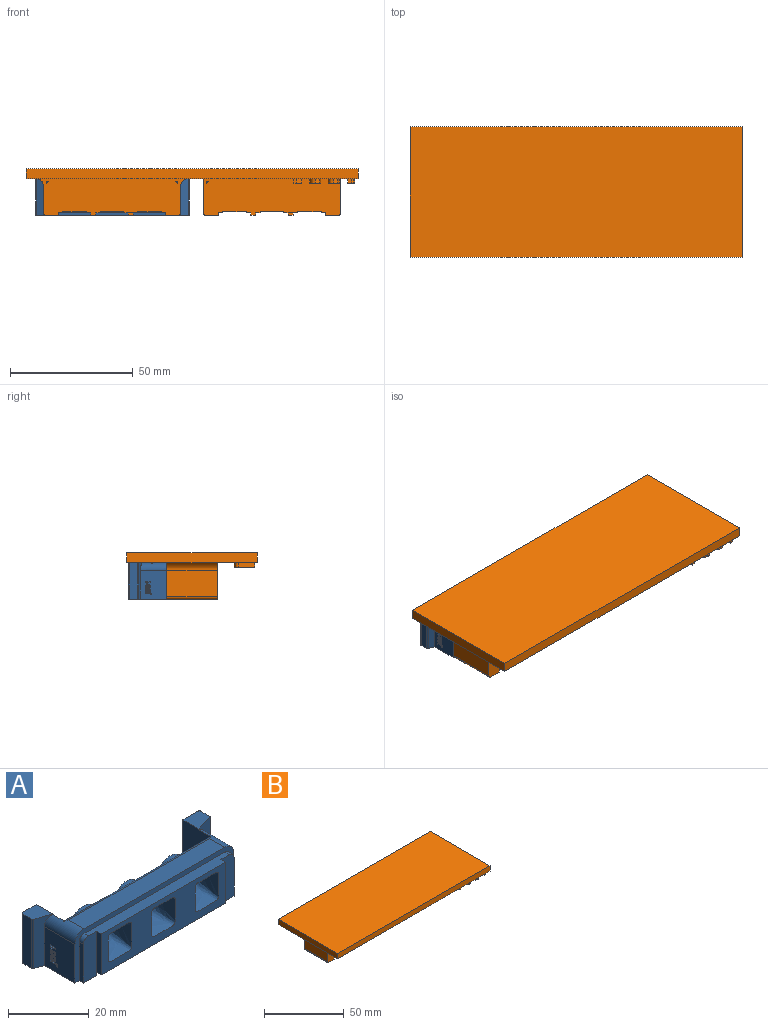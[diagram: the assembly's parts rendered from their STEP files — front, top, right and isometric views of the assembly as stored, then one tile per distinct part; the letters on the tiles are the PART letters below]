
ASSEMBLY  parts=2 mates=1
PART A: 118 faces, bbox 63x19.4x15.4 mm
  f0: plane 11.78x10.74mm, normal (-1,0,0), area 119.5mm2, adj f11,f26,f39,f49,f60,f61,f62,f63
  f1: plane 44.18x12.95mm, normal (0,-1,0), area 333.4mm2, adj f4,f54,f55,f56,f57,f58,f59
  f2: plane 13.48x4.58mm, normal (0,-1,0), area 61.1mm2, adj f4,f11,f45,f46,f47,f56
  f3: cylinder r=1.7mm len=1.7mm, axis (0,-1,0), area 4mm2, adj f4,f21,f48,f49
  f4: plane 49.45x3.15mm, normal (0,0,1), area 146.3mm2, adj f1,f2,f3,f21,f46,f49,f55,f56
  f5: plane 2.03x1.02mm, normal (0,-1,0), area 2.1mm2, adj f11,f43,f44,f54
  f6: plane 2.03x1.02mm, normal (0,-1,0), area 2.1mm2, adj f11,f41,f42,f54
  f7: cylinder r=3.17mm len=6.35mm, axis (0,-1,0), area 89.2mm2, adj f30,f57
  f8: cylinder r=3.17mm len=6.35mm, axis (0,-1,0), area 89.2mm2, adj f34,f59
  f9: cylinder r=3.17mm len=6.35mm, axis (0,-1,0), area 89.2mm2, adj f32,f58
  f10: plane 11.78x10.74mm, normal (1,0,0), area 126.5mm2, adj f11,f27,f38,f49
  f11: plane 62.5x17.24mm, normal (0,0,-1), area 324.6mm2, adj f0,f2,f5,f6,f10,f12,f14,f16
  f12: plane 13.21x1.02mm, normal (0,-1,0), area 13.4mm2, adj f11,f13,f44,f45
  f13: plane 13.21x4.57mm, normal (0,0,-1), area 60.4mm2, adj f12,f44,f45,f54
  f14: plane 13.21x1.02mm, normal (0,-1,0), area 13.4mm2, adj f11,f15,f42,f43
  f15: plane 13.21x4.57mm, normal (0,0,-1), area 60.4mm2, adj f14,f42,f43,f54
  f16: plane 13.21x1.02mm, normal (0,-1,0), area 13.4mm2, adj f11,f17,f40,f41
  f17: plane 13.21x4.57mm, normal (0,0,-1), area 60.4mm2, adj f16,f40,f41,f54
  f18: plane 49.45x5.36mm, normal (0,0,1), area 265mm2, adj f37,f38,f39,f49
  f19: plane 5.69x5.33mm, normal (0,0,1), area 25.7mm2, adj f22,f25,f26,f29,f51,f52
  f20: plane 51.44x13.94mm, normal (0,1,0), area 530.7mm2, adj f11,f22,f23,f31,f33,f35,f37
  f21: plane 13.48x4.58mm, normal (0,-1,0), area 61.1mm2, adj f3,f4,f11,f40,f48,f55
  f22: plane 14.95x9.83mm, normal (1,0,0), area 139.5mm2, adj f11,f19,f20,f26,f37,f39,f51
  f23: plane 14.95x9.83mm, normal (-1,0,0), area 139.5mm2, adj f11,f20,f27,f36,f37,f38,f50
  f24: plane 14.95x3.11mm, normal (1,0,0), area 46.5mm2, adj f11,f28,f36,f53
  f25: plane 14.95x3.12mm, normal (-1,0,0), area 46.7mm2, adj f11,f19,f29,f52
  f26: plane 15.27x5.29mm, normal (-0.3,-0.95,0), area 46mm2, adj f0,f11,f19,f22,f29,f39
  f27: plane 15.23x5.64mm, normal (0.27,-0.96,0), area 51.6mm2, adj f10,f11,f23,f28,f36,f38
  f28: cylinder r=0.51mm len=14.95mm, axis (0,0,-1), area 9.8mm2, adj f11,f24,f27,f36
  f29: cylinder r=0.51mm len=14.95mm, axis (0,0,-1), area 9.6mm2, adj f11,f19,f25,f26
  f30: plane 8.89x8.89mm, normal (0,1,0), area 30.4mm2, adj f7,f31
  f31: cylinder r=4.45mm len=8.89mm, axis (0,-1,0), area 96.5mm2, adj f20,f30
  f32: plane 8.89x8.89mm, normal (0,1,0), area 30.4mm2, adj f9,f33
  f33: cylinder r=4.45mm len=8.89mm, axis (0,-1,0), area 96.5mm2, adj f20,f32
  f34: plane 8.89x8.89mm, normal (0,1,0), area 30.4mm2, adj f8,f35
  f35: cylinder r=4.45mm len=8.89mm, axis (0,-1,0), area 96.5mm2, adj f20,f34
  f36: plane 5.74x5.61mm, normal (0,0,1), area 27.5mm2, adj f23,f24,f27,f28,f50,f53
  f37: cylinder r=1.02mm len=51.44mm, axis (1,0,0), area 81.5mm2, adj f18,f20,f22,f23,f38,f39
  f38: cylinder r=3.17mm len=10.74mm, axis (0,-1,0), area 47.2mm2, adj f10,f18,f23,f27,f37,f49
  f39: cylinder r=3.17mm len=10.74mm, axis (0,1,0), area 47mm2, adj f0,f18,f22,f26,f37,f49
  f40: plane 4.57x1.02mm, normal (1,0,0), area 4.6mm2, adj f11,f16,f17,f21
  f41: plane 4.57x1.02mm, normal (-1,0,0), area 4.6mm2, adj f6,f11,f16,f17
  f42: plane 4.57x1.02mm, normal (1,0,0), area 4.6mm2, adj f6,f11,f14,f15
  f43: plane 4.57x1.02mm, normal (-1,0,0), area 4.6mm2, adj f5,f11,f14,f15
  f44: plane 4.57x1.02mm, normal (1,0,0), area 4.6mm2, adj f5,f11,f12,f13
  f45: plane 4.57x1.02mm, normal (-1,0,0), area 4.6mm2, adj f2,f11,f12,f13
  f46: cylinder r=1.7mm len=1.7mm, axis (0,-1,0), area 4mm2, adj f2,f4,f47,f49
  f47: plane 11.78x1.5mm, normal (1,0,0), area 17.7mm2, adj f2,f11,f46,f49
  f48: plane 11.78x1.5mm, normal (-1,0,0), area 17.7mm2, adj f3,f11,f21,f49
  f49: plane 55.8x14.95mm, normal (0,-1,0), area 119mm2, adj f0,f3,f4,f10,f11,f18,f38,f39
  f50: plane 14.95x5.23mm, normal (0,1,0), area 78.2mm2, adj f11,f23,f36,f53
  f51: plane 14.95x4.82mm, normal (0,1,0), area 72.1mm2, adj f11,f19,f22,f52
  f52: cylinder r=0.51mm len=14.95mm, axis (0,0,-1), area 11.9mm2, adj f11,f19,f25,f51
  f53: cylinder r=0.51mm len=14.95mm, axis (0,0,-1), area 11.9mm2, adj f11,f24,f36,f50
  f54: plane 43.69x1.65mm, normal (0,0,-1), area 72.1mm2, adj f1,f5,f6,f13,f15,f17,f55,f56
  f55: plane 12.46x1.65mm, normal (-1,0,0), area 20.6mm2, adj f1,f4,f21,f54
  f56: plane 12.46x1.65mm, normal (1,0,0), area 20.6mm2, adj f1,f2,f4,f54
  f57: bspline ~8.64x8.51mm, area 223.4mm2, adj f1,f7
  f58: bspline ~8.64x8.51mm, area 223.4mm2, adj f1,f9
  f59: bspline ~8.64x8.51mm, area 223.4mm2, adj f1,f8
  f60: plane 1x0.42mm, normal (0,1,0), area 0.4mm2, adj f0,f61,f69,f70
  f61: plane 1.98x1mm, normal (0,0,-1), area 2mm2, adj f0,f60,f62,f70
  f62: plane 1x0.34mm, normal (0,-1,0), area 0.3mm2, adj f0,f61,f63,f70
  f63: plane 1x0.64mm, normal (0,-0.78,0.62), area 0.8mm2, adj f0,f62,f64,f70
  f64: plane 1x0.25mm, normal (0,0.63,0.78), area 0.3mm2, adj f0,f63,f65,f70
  f65: plane 1x0.23mm, normal (0,0.78,-0.63), area 0.3mm2, adj f0,f64,f66,f70
  f66: extruded ~1x0.15mm, area 0.2mm2, adj f0,f65,f67,f70
  f67: plane 1x0.21mm, normal (0,-0.03,1), area 0.2mm2, adj f0,f66,f68,f70
  f68: plane 1x0.19mm, normal (0,-0.02,1), area 0.2mm2, adj f0,f67,f69,f70
  f69: plane 1.15x1mm, normal (0,0,1), area 1.1mm2, adj f0,f60,f68,f70
  f70: plane 1.98x0.98mm, normal (-1,0,0), area 1mm2, adj f60,f61,f62,f63,f64,f65,f66,f67
  f71: extruded ~1x0.52mm, area 0.5mm2, adj f72,f86,f87,f116
  f72: extruded ~1x0.52mm, area 0.5mm2, adj f71,f73,f87,f116
  f73: extruded ~1x0.21mm, area 0.3mm2, adj f72,f74,f87,f116
  f74: extruded ~1x0.21mm, area 0.3mm2, adj f73,f75,f87,f116
  f75: extruded ~1x0.52mm, area 0.5mm2, adj f74,f76,f87,f116
  f76: extruded ~1x0.52mm, area 0.5mm2, adj f75,f77,f87,f116
  f77: extruded ~1x0.21mm, area 0.3mm2, adj f76,f86,f87,f116
  f78: extruded ~1x0.77mm, area 0.8mm2, adj f0,f79,f85,f87
  f79: extruded ~1x0.76mm, area 0.8mm2, adj f0,f78,f80,f87
  f80: extruded ~1x0.52mm, area 0.6mm2, adj f0,f79,f81,f87
  f81: extruded ~1x0.52mm, area 0.6mm2, adj f0,f80,f82,f87
  f82: extruded ~1x0.77mm, area 0.8mm2, adj f0,f81,f83,f87
  f83: extruded ~1x0.76mm, area 0.8mm2, adj f0,f82,f84,f87
  f84: extruded ~1x0.52mm, area 0.6mm2, adj f0,f83,f85,f87
  f85: extruded ~1x0.52mm, area 0.6mm2, adj f0,f78,f84,f87
  f86: extruded ~1x0.21mm, area 0.3mm2, adj f71,f77,f87,f116
  f87: plane 2.04x1.39mm, normal (-1,0,0), area 1.7mm2, adj f71,f72,f73,f74,f75,f76,f77,f78
  f88: extruded ~1x0.52mm, area 0.5mm2, adj f89,f103,f104,f117
  f89: extruded ~1x0.52mm, area 0.5mm2, adj f88,f90,f104,f117
  f90: extruded ~1x0.21mm, area 0.3mm2, adj f89,f91,f104,f117
  f91: extruded ~1x0.21mm, area 0.3mm2, adj f90,f92,f104,f117
  f92: extruded ~1x0.52mm, area 0.5mm2, adj f91,f93,f104,f117
  f93: extruded ~1x0.52mm, area 0.5mm2, adj f92,f94,f104,f117
  f94: extruded ~1x0.21mm, area 0.3mm2, adj f93,f103,f104,f117
  f95: extruded ~1x0.77mm, area 0.8mm2, adj f0,f96,f102,f104
  f96: extruded ~1x0.76mm, area 0.8mm2, adj f0,f95,f97,f104
  f97: extruded ~1x0.52mm, area 0.6mm2, adj f0,f96,f98,f104
  f98: extruded ~1x0.52mm, area 0.6mm2, adj f0,f97,f99,f104
  f99: extruded ~1x0.77mm, area 0.8mm2, adj f0,f98,f100,f104
  f100: extruded ~1x0.76mm, area 0.8mm2, adj f0,f99,f101,f104
  f101: extruded ~1x0.52mm, area 0.6mm2, adj f0,f100,f102,f104
  f102: extruded ~1x0.52mm, area 0.6mm2, adj f0,f95,f101,f104
  f103: extruded ~1x0.21mm, area 0.3mm2, adj f88,f94,f104,f117
  f104: plane 2.04x1.39mm, normal (-1,0,0), area 1.7mm2, adj f88,f89,f90,f91,f92,f93,f94,f95
  f105: extruded ~1x0.25mm, area 0.3mm2, adj f0,f106,f114,f115
  f106: extruded ~1x0.47mm, area 0.5mm2, adj f0,f105,f107,f115
  f107: extruded ~1x0.53mm, area 0.6mm2, adj f0,f106,f108,f115
  f108: plane 1.86x1mm, normal (0,0,-1), area 1.9mm2, adj f0,f107,f109,f115
  f109: plane 1x0.42mm, normal (0,-1,0), area 0.4mm2, adj f0,f108,f110,f115
  f110: plane 1.86x1mm, normal (0,0,1), area 1.9mm2, adj f0,f109,f111,f115
  f111: extruded ~1x0.27mm, area 0.3mm2, adj f0,f110,f112,f115
  f112: extruded ~1x0.2mm, area 0.2mm2, adj f0,f111,f113,f115
  f113: extruded ~1x0.2mm, area 0.2mm2, adj f0,f112,f114,f115
  f114: plane 1x0.35mm, normal (0,0,1), area 0.3mm2, adj f0,f105,f113,f115
  f115: plane 2.57x0.88mm, normal (-1,0,0), area 1.2mm2, adj f105,f106,f107,f108,f109,f110,f111,f112
  f116: plane 1.36x0.55mm, normal (-1,0,0), area 0.6mm2, adj f71,f72,f73,f74,f75,f76,f77,f86
  f117: plane 1.36x0.55mm, normal (-1,0,0), area 0.6mm2, adj f88,f89,f90,f91,f92,f93,f94,f103
PART B: 188 faces, bbox 135.1x53.1x19.1 mm
  f0: plane 135x53mm, normal (0,0,-1), area 4658.1mm2, adj f20,f61,f81,f82,f83,f122,f123,f124
  f1: plane 43.69x13.68mm, normal (0,1,0), area 279.1mm2, adj f2,f5,f7,f8,f9,f10,f12,f13
  f2: plane 53.24x3.15mm, normal (0,0,-1), area 152mm2, adj f1,f3,f6,f14,f36,f55,f57,f61
  f3: plane 13.68x4.78mm, normal (0,1,0), area 65.3mm2, adj f2,f31,f36,f55
  f4: torus R=2.16mm, axis (0,1,0), area 0.4mm2, adj f20,f56,f58
  f5: plane 17.4x1.78mm, normal (0,0,-1), area 30.9mm2, adj f1,f7,f14,f20
  f6: plane 13.68x4.78mm, normal (0,1,0), area 65.3mm2, adj f2,f11,f14,f57
  f7: plane 17.4x0.43mm, normal (1,0,0), area 7.5mm2, adj f1,f5,f20,f25
  f8: plane 17.4x0.43mm, normal (-1,0,0), area 7.5mm2, adj f1,f12,f20,f29
  f9: plane 17.4x0.43mm, normal (1,0,0), area 7.5mm2, adj f1,f12,f20,f30
  f10: plane 17.4x0.43mm, normal (-1,0,0), area 7.5mm2, adj f1,f13,f20,f30
  f11: plane 20.55x5.04mm, normal (0,0,-1), area 96.4mm2, adj f6,f14,f20,f41,f57,f61
  f12: plane 17.4x5.59mm, normal (0,0,-1), area 61.9mm2, adj f1,f8,f9,f20,f49,f50,f51
  f13: plane 17.4x1.78mm, normal (0,0,-1), area 30.9mm2, adj f1,f10,f20,f36
  f14: plane 19.05x13.68mm, normal (1,0,0), area 40.3mm2, adj f1,f2,f5,f6,f11,f20
  f15: plane 14.25x10.51mm, normal (-1,0.02,0), area 126.2mm2, adj f1,f26,f30,f32,f44,f47
  f16: plane 14.25x10.51mm, normal (1,0.02,0), area 126.2mm2, adj f1,f26,f30,f32,f44,f47
  f17: plane 14.25x10.51mm, normal (-1,0.02,0), area 126.2mm2, adj f1,f27,f29,f33,f43,f46
  f18: plane 14.25x10.51mm, normal (1,0.02,0), area 126.2mm2, adj f1,f27,f29,f33,f43,f46
  f19: plane 14.25x10.51mm, normal (-1,0.02,0), area 126.2mm2, adj f1,f25,f28,f35,f42,f45
  f20: plane 62.15x14.95mm, normal (0,-1,0), area 782.9mm2, adj f0,f4,f5,f7,f8,f9,f10,f11
  f21: plane 20.55x10.76mm, normal (-1,0,0), area 221.2mm2, adj f20,f41,f61,f187
  f22: plane 20.55x10.76mm, normal (1,0,0), area 221.2mm2, adj f20,f39,f61,f186
  f23: plane 17.4x0.43mm, normal (-1,0,0), area 7.5mm2, adj f1,f20,f25,f37
  f24: plane 17.4x0.43mm, normal (1,0,0), area 7.5mm2, adj f1,f20,f29,f38
  f25: plane 17.4x9.65mm, normal (0,0,-1), area 51.3mm2, adj f1,f7,f19,f20,f23,f34,f35
  f26: plane 8.45x0.86mm, normal (0,0.02,-1), area 7.3mm2, adj f1,f15,f16,f44
  f27: plane 8.45x0.86mm, normal (0,0.02,-1), area 7.3mm2, adj f1,f17,f18,f43
  f28: plane 8.45x0.86mm, normal (0,0.02,-1), area 7.3mm2, adj f1,f19,f34,f42
  f29: plane 17.4x9.65mm, normal (0,0,-1), area 51.3mm2, adj f1,f8,f17,f18,f20,f24,f33
  f30: plane 17.4x9.65mm, normal (0,0,-1), area 51.3mm2, adj f1,f9,f10,f15,f16,f20,f32
  f31: plane 20.55x5.04mm, normal (0,0,-1), area 96.4mm2, adj f3,f20,f36,f39,f55,f61
  f32: plane 7.95x5.84mm, normal (0,1,0), area 46.4mm2, adj f15,f16,f30,f47
  f33: plane 7.95x5.84mm, normal (0,1,0), area 46.4mm2, adj f17,f18,f29,f46
  f34: plane 14.25x10.51mm, normal (1,0.02,0), area 126.2mm2, adj f1,f25,f28,f35,f42,f45
  f35: plane 7.95x5.84mm, normal (0,1,0), area 46.4mm2, adj f19,f25,f34,f45
  f36: plane 19.05x13.68mm, normal (-1,0,0), area 40.3mm2, adj f1,f2,f3,f13,f20,f31
  f37: plane 17.4x1.78mm, normal (0,0,-1), area 30.9mm2, adj f1,f20,f23,f53
  f38: plane 17.4x1.78mm, normal (0,0,-1), area 30.9mm2, adj f1,f20,f24,f54
  f39: cylinder r=1.02mm len=20.55mm, axis (0,1,0), area 32.8mm2, adj f20,f22,f31,f61
  f40: torus R=2.16mm, axis (0,1,0), area 0.4mm2, adj f20,f59,f60
  f41: cylinder r=1.02mm len=20.55mm, axis (0,-1,0), area 32.8mm2, adj f11,f20,f21,f61
  f42: plane 8.42x5mm, normal (0,0.61,-0.79), area 52.8mm2, adj f19,f28,f34,f45
  f43: plane 8.42x5mm, normal (0,0.61,-0.79), area 52.8mm2, adj f17,f18,f27,f46
  f44: plane 8.42x5mm, normal (0,0.61,-0.79), area 52.8mm2, adj f15,f16,f26,f47
  f45: cylinder r=4.25mm len=8.36mm, axis (1,0,0), area 96.9mm2, adj f19,f34,f35,f42
  f46: cylinder r=4.25mm len=8.36mm, axis (1,0,0), area 96.9mm2, adj f17,f18,f33,f43
  f47: cylinder r=4.25mm len=8.36mm, axis (1,0,0), area 96.9mm2, adj f15,f16,f32,f44
  f48: plane 17.36x2.03mm, normal (0,0,-1), area 35.3mm2, adj f1,f49,f50,f51
  f49: plane 2.03x1.02mm, normal (0,-1,0), area 2.1mm2, adj f12,f48,f50,f51
  f50: plane 17.36x1.02mm, normal (-1,0,0), area 17.6mm2, adj f1,f12,f48,f49
  f51: plane 17.36x1.02mm, normal (1,0,0), area 17.6mm2, adj f1,f12,f48,f49
  f52: plane 17.4x2.03mm, normal (0,0,-1), area 35.4mm2, adj f1,f20,f53,f54
  f53: plane 17.4x1.02mm, normal (-1,0,0), area 17.7mm2, adj f1,f20,f37,f52
  f54: plane 17.4x1.02mm, normal (1,0,0), area 17.7mm2, adj f1,f20,f38,f52
  f55: plane 13.68x1.5mm, normal (-1,0,0), area 20.5mm2, adj f2,f3,f31,f61
  f56: plane 0.98x0.26mm, normal (0,0,-1), area 0mm2, adj f4,f20,f58
  f57: plane 13.68x1.5mm, normal (1,0,0), area 20.5mm2, adj f2,f6,f11,f61
  f58: plane 0.98x0.26mm, normal (-1,0,0), area 0mm2, adj f4,f20,f56
  f59: plane 0.98x0.26mm, normal (0,0,-1), area 0mm2, adj f20,f40,f60
  f60: plane 0.98x0.26mm, normal (1,0,0), area 0mm2, adj f20,f40,f59
  f61: plane 62.15x14.95mm, normal (0,1,0), area 110.2mm2, adj f0,f2,f11,f21,f22,f31,f39,f41
  f62: plane 43.69x13.68mm, normal (0,1,0), area 279.1mm2, adj f63,f66,f68,f69,f70,f71,f73,f74
  f63: plane 53.24x3.15mm, normal (0,0,-1), area 152mm2, adj f62,f64,f67,f75,f97,f116,f118,f122
  f64: plane 13.68x4.78mm, normal (0,1,0), area 65.3mm2, adj f63,f92,f97,f116
  f65: torus R=2.16mm, axis (0,1,0), area 0.4mm2, adj f81,f117,f119
  f66: plane 17.4x1.78mm, normal (0,0,-1), area 30.9mm2, adj f62,f68,f75,f81
  f67: plane 13.68x4.78mm, normal (0,1,0), area 65.3mm2, adj f63,f72,f75,f118
  f68: plane 17.4x0.43mm, normal (1,0,0), area 7.5mm2, adj f62,f66,f81,f86
  f69: plane 17.4x0.43mm, normal (-1,0,0), area 7.5mm2, adj f62,f73,f81,f90
  f70: plane 17.4x0.43mm, normal (1,0,0), area 7.5mm2, adj f62,f73,f81,f91
  f71: plane 17.4x0.43mm, normal (-1,0,0), area 7.5mm2, adj f62,f74,f81,f91
  f72: plane 20.55x5.04mm, normal (0,0,-1), area 96.4mm2, adj f67,f75,f81,f102,f118,f122
  f73: plane 17.4x5.59mm, normal (0,0,-1), area 61.9mm2, adj f62,f69,f70,f81,f110,f111,f112
  f74: plane 17.4x1.78mm, normal (0,0,-1), area 30.9mm2, adj f62,f71,f81,f97
  f75: plane 19.05x13.68mm, normal (1,0,0), area 40.3mm2, adj f62,f63,f66,f67,f72,f81
  f76: plane 14.25x10.51mm, normal (-1,0.02,0), area 126.2mm2, adj f62,f87,f91,f93,f105,f108
  f77: plane 14.25x10.51mm, normal (1,0.02,0), area 126.2mm2, adj f62,f87,f91,f93,f105,f108
  f78: plane 14.25x10.51mm, normal (-1,0.02,0), area 126.2mm2, adj f62,f88,f90,f94,f104,f107
  f79: plane 14.25x10.51mm, normal (1,0.02,0), area 126.2mm2, adj f62,f88,f90,f94,f104,f107
  f80: plane 14.25x10.51mm, normal (-1,0.02,0), area 126.2mm2, adj f62,f86,f89,f96,f103,f106
  f81: plane 55.8x14.95mm, normal (0,-1,0), area 778.6mm2, adj f0,f65,f66,f68,f69,f70,f71,f72
  f82: plane 20.55x13.94mm, normal (-1,0,0), area 286.4mm2, adj f0,f81,f102,f122
  f83: plane 20.55x13.94mm, normal (1,0,0), area 286.4mm2, adj f0,f81,f100,f122
  f84: plane 17.4x0.43mm, normal (-1,0,0), area 7.5mm2, adj f62,f81,f86,f98
  f85: plane 17.4x0.43mm, normal (1,0,0), area 7.5mm2, adj f62,f81,f90,f99
  f86: plane 17.4x9.65mm, normal (0,0,-1), area 51.3mm2, adj f62,f68,f80,f81,f84,f95,f96
  f87: plane 8.45x0.86mm, normal (0,0.02,-1), area 7.3mm2, adj f62,f76,f77,f105
  f88: plane 8.45x0.86mm, normal (0,0.02,-1), area 7.3mm2, adj f62,f78,f79,f104
  f89: plane 8.45x0.86mm, normal (0,0.02,-1), area 7.3mm2, adj f62,f80,f95,f103
  f90: plane 17.4x9.65mm, normal (0,0,-1), area 51.3mm2, adj f62,f69,f78,f79,f81,f85,f94
  f91: plane 17.4x9.65mm, normal (0,0,-1), area 51.3mm2, adj f62,f70,f71,f76,f77,f81,f93
  f92: plane 20.55x5.04mm, normal (0,0,-1), area 96.4mm2, adj f64,f81,f97,f100,f116,f122
  f93: plane 7.95x5.84mm, normal (0,1,0), area 46.4mm2, adj f76,f77,f91,f108
  f94: plane 7.95x5.84mm, normal (0,1,0), area 46.4mm2, adj f78,f79,f90,f107
  f95: plane 14.25x10.51mm, normal (1,0.02,0), area 126.2mm2, adj f62,f86,f89,f96,f103,f106
  f96: plane 7.95x5.84mm, normal (0,1,0), area 46.4mm2, adj f80,f86,f95,f106
  f97: plane 19.05x13.68mm, normal (-1,0,0), area 40.3mm2, adj f62,f63,f64,f74,f81,f92
  f98: plane 17.4x1.78mm, normal (0,0,-1), area 30.9mm2, adj f62,f81,f84,f114
  f99: plane 17.4x1.78mm, normal (0,0,-1), area 30.9mm2, adj f62,f81,f85,f115
  f100: cylinder r=1.02mm len=20.55mm, axis (0,1,0), area 32.8mm2, adj f81,f83,f92,f122
  f101: torus R=2.16mm, axis (0,1,0), area 0.4mm2, adj f81,f120,f121
  f102: cylinder r=1.02mm len=20.55mm, axis (0,-1,0), area 32.8mm2, adj f72,f81,f82,f122
  f103: plane 8.42x5mm, normal (0,0.61,-0.79), area 52.8mm2, adj f80,f89,f95,f106
  f104: plane 8.42x5mm, normal (0,0.61,-0.79), area 52.8mm2, adj f78,f79,f88,f107
  f105: plane 8.42x5mm, normal (0,0.61,-0.79), area 52.8mm2, adj f76,f77,f87,f108
  f106: cylinder r=4.25mm len=8.36mm, axis (1,0,0), area 96.9mm2, adj f80,f95,f96,f103
  f107: cylinder r=4.25mm len=8.36mm, axis (1,0,0), area 96.9mm2, adj f78,f79,f94,f104
  f108: cylinder r=4.25mm len=8.36mm, axis (1,0,0), area 96.9mm2, adj f76,f77,f93,f105
  f109: plane 17.36x2.03mm, normal (0,0,-1), area 35.3mm2, adj f62,f110,f111,f112
  f110: plane 2.03x1.02mm, normal (0,-1,0), area 2.1mm2, adj f73,f109,f111,f112
  f111: plane 17.36x1.02mm, normal (-1,0,0), area 17.6mm2, adj f62,f73,f109,f110
  f112: plane 17.36x1.02mm, normal (1,0,0), area 17.6mm2, adj f62,f73,f109,f110
  f113: plane 17.4x2.03mm, normal (0,0,-1), area 35.4mm2, adj f62,f81,f114,f115
  f114: plane 17.4x1.02mm, normal (-1,0,0), area 17.7mm2, adj f62,f81,f98,f113
  f115: plane 17.4x1.02mm, normal (1,0,0), area 17.7mm2, adj f62,f81,f99,f113
  f116: plane 13.68x1.5mm, normal (-1,0,0), area 20.5mm2, adj f63,f64,f92,f122
  f117: plane 0.98x0.26mm, normal (0,0,-1), area 0mm2, adj f65,f81,f119
  f118: plane 13.68x1.5mm, normal (1,0,0), area 20.5mm2, adj f63,f67,f72,f122
  f119: plane 0.98x0.26mm, normal (-1,0,0), area 0mm2, adj f65,f81,f117
  f120: plane 0.98x0.26mm, normal (0,0,-1), area 0mm2, adj f81,f101,f121
  f121: plane 0.98x0.26mm, normal (1,0,0), area 0mm2, adj f81,f101,f120
  f122: plane 55.8x14.95mm, normal (0,1,0), area 105.8mm2, adj f0,f63,f72,f82,f83,f92,f100,f102
  f123: plane 53x4mm, normal (-1,0,0), area 212mm2, adj f0,f124,f126,f127
  f124: plane 135x4mm, normal (0,-1,0), area 540mm2, adj f0,f123,f125,f127
  f125: plane 53x4mm, normal (1,0,0), area 212mm2, adj f0,f124,f126,f127
  f126: plane 135x4mm, normal (0,1,0), area 540mm2, adj f0,f123,f125,f127
  f127: plane 135x53mm, normal (0,0,1), area 7155mm2, adj f123,f124,f125,f126
  f128: extruded ~2x1.53mm, area 3.4mm2, adj f0,f129,f137,f138
  f129: extruded ~2x0.81mm, area 1.6mm2, adj f0,f128,f130,f138
  f130: plane 2x1.14mm, normal (1,0,0), area 2.3mm2, adj f0,f129,f131,f138
  f131: extruded ~2x0.64mm, area 1.3mm2, adj f0,f130,f132,f138
  f132: extruded ~2x0.64mm, area 1.5mm2, adj f0,f131,f133,f138
  f133: extruded ~2x0.88mm, area 1.8mm2, adj f0,f132,f134,f138
  f134: plane 6.04x2mm, normal (1,0,0), area 12.1mm2, adj f0,f133,f135,f138
  f135: plane 2x1.37mm, normal (0,-1,0), area 2.7mm2, adj f0,f134,f136,f138
  f136: plane 6.03x2mm, normal (-1,0,0), area 12.1mm2, adj f0,f135,f137,f138
  f137: extruded ~2x1.72mm, area 3.7mm2, adj f0,f128,f136,f138
  f138: plane 8.34x2.85mm, normal (0,0,-1), area 12.4mm2, adj f128,f129,f130,f131,f132,f133,f134,f135
  f139: extruded ~2.48x2mm, area 5.2mm2, adj f0,f140,f154,f155
  f140: extruded ~2.5x2mm, area 5.2mm2, adj f0,f139,f141,f155
  f141: extruded ~2x1.7mm, area 3.9mm2, adj f0,f140,f142,f155
  f142: extruded ~2x1.68mm, area 3.9mm2, adj f0,f141,f143,f155
  f143: extruded ~2.47x2mm, area 5.1mm2, adj f0,f142,f144,f155
  f144: extruded ~2.52x2mm, area 5.2mm2, adj f0,f143,f145,f155
  f145: extruded ~2x1.7mm, area 3.9mm2, adj f0,f144,f154,f155
  f146: extruded ~2x1.7mm, area 3.5mm2, adj f147,f153,f155,f156
  f147: extruded ~2x1.7mm, area 3.4mm2, adj f146,f148,f155,f156
  f148: extruded ~2x0.69mm, area 1.8mm2, adj f147,f149,f155,f156
  f149: extruded ~2x0.69mm, area 1.8mm2, adj f148,f150,f155,f156
  f150: extruded ~2x1.69mm, area 3.4mm2, adj f149,f151,f155,f156
  f151: extruded ~2x1.7mm, area 3.5mm2, adj f150,f152,f155,f156
  f152: extruded ~2x0.69mm, area 1.8mm2, adj f151,f153,f155,f156
  f153: extruded ~2x0.69mm, area 1.8mm2, adj f146,f152,f155,f156
  f154: extruded ~2x1.69mm, area 3.9mm2, adj f0,f139,f145,f155
  f155: plane 6.64x4.51mm, normal (0,0,-1), area 18.2mm2, adj f139,f140,f141,f142,f143,f144,f145,f146
  f156: plane 4.43x1.79mm, normal (0,0,-1), area 6.8mm2, adj f146,f147,f148,f149,f150,f151,f152,f153
  f157: extruded ~2.48x2mm, area 5.2mm2, adj f0,f158,f172,f173
  f158: extruded ~2.5x2mm, area 5.2mm2, adj f0,f157,f159,f173
  f159: extruded ~2x1.7mm, area 3.9mm2, adj f0,f158,f160,f173
  f160: extruded ~2x1.68mm, area 3.9mm2, adj f0,f159,f161,f173
  f161: extruded ~2.47x2mm, area 5.1mm2, adj f0,f160,f162,f173
  f162: extruded ~2.52x2mm, area 5.2mm2, adj f0,f161,f163,f173
  f163: extruded ~2x1.7mm, area 3.9mm2, adj f0,f162,f172,f173
  f164: extruded ~2x1.7mm, area 3.5mm2, adj f165,f171,f173,f174
  f165: extruded ~2x1.7mm, area 3.4mm2, adj f164,f166,f173,f174
  f166: extruded ~2x0.69mm, area 1.8mm2, adj f165,f167,f173,f174
  f167: extruded ~2x0.69mm, area 1.8mm2, adj f166,f168,f173,f174
  f168: extruded ~2x1.69mm, area 3.4mm2, adj f167,f169,f173,f174
  f169: extruded ~2x1.7mm, area 3.5mm2, adj f168,f170,f173,f174
  f170: extruded ~2x0.69mm, area 1.8mm2, adj f169,f171,f173,f174
  f171: extruded ~2x0.69mm, area 1.8mm2, adj f164,f170,f173,f174
  f172: extruded ~2x1.69mm, area 3.9mm2, adj f0,f157,f163,f173
  f173: plane 6.64x4.51mm, normal (0,0,-1), area 18.2mm2, adj f157,f158,f159,f160,f161,f162,f163,f164
  f174: plane 4.43x1.79mm, normal (0,0,-1), area 6.8mm2, adj f164,f165,f166,f167,f168,f169,f170,f171
  f175: plane 6.45x2mm, normal (-1,0,0), area 12.9mm2, adj f0,f176,f184,f185
  f176: plane 2x1.36mm, normal (0,1,0), area 2.7mm2, adj f0,f175,f177,f185
  f177: plane 3.73x2mm, normal (1,0,0), area 7.5mm2, adj f0,f176,f178,f185
  f178: plane 2x0.61mm, normal (1,-0.02,0), area 1.2mm2, adj f0,f177,f179,f185
  f179: plane 2x0.67mm, normal (1,-0.03,0), area 1.3mm2, adj f0,f178,f180,f185
  f180: extruded ~2x0.47mm, area 1.3mm2, adj f0,f179,f181,f185
  f181: plane 2x0.74mm, normal (-0.63,0.78,0), area 1.9mm2, adj f0,f180,f182,f185
  f182: plane 2x0.82mm, normal (0.78,0.63,0), area 2.1mm2, adj f0,f181,f183,f185
  f183: plane 2.08x2mm, normal (0.62,-0.78,0), area 5.3mm2, adj f0,f182,f184,f185
  f184: plane 2x1.12mm, normal (0,-1,0), area 2.2mm2, adj f0,f175,f183,f185
  f185: plane 6.45x3.2mm, normal (0,0,-1), area 10.7mm2, adj f175,f176,f177,f178,f179,f180,f181,f182
  f186: cylinder r=3.17mm len=20.55mm, axis (0,1,0), area 102.5mm2, adj f0,f20,f22,f61
  f187: cylinder r=3.17mm len=20.55mm, axis (0,-1,0), area 102.5mm2, adj f0,f20,f21,f61
PLACE A t=(-16.91,9.34,-7.53)mm
PLACE B t=(-16.91,9.34,-7.53)mm
MATE fastened A.f49 <-> B.f61  axis (0,-1,0) through (10.4,12.49,7.42)mm
